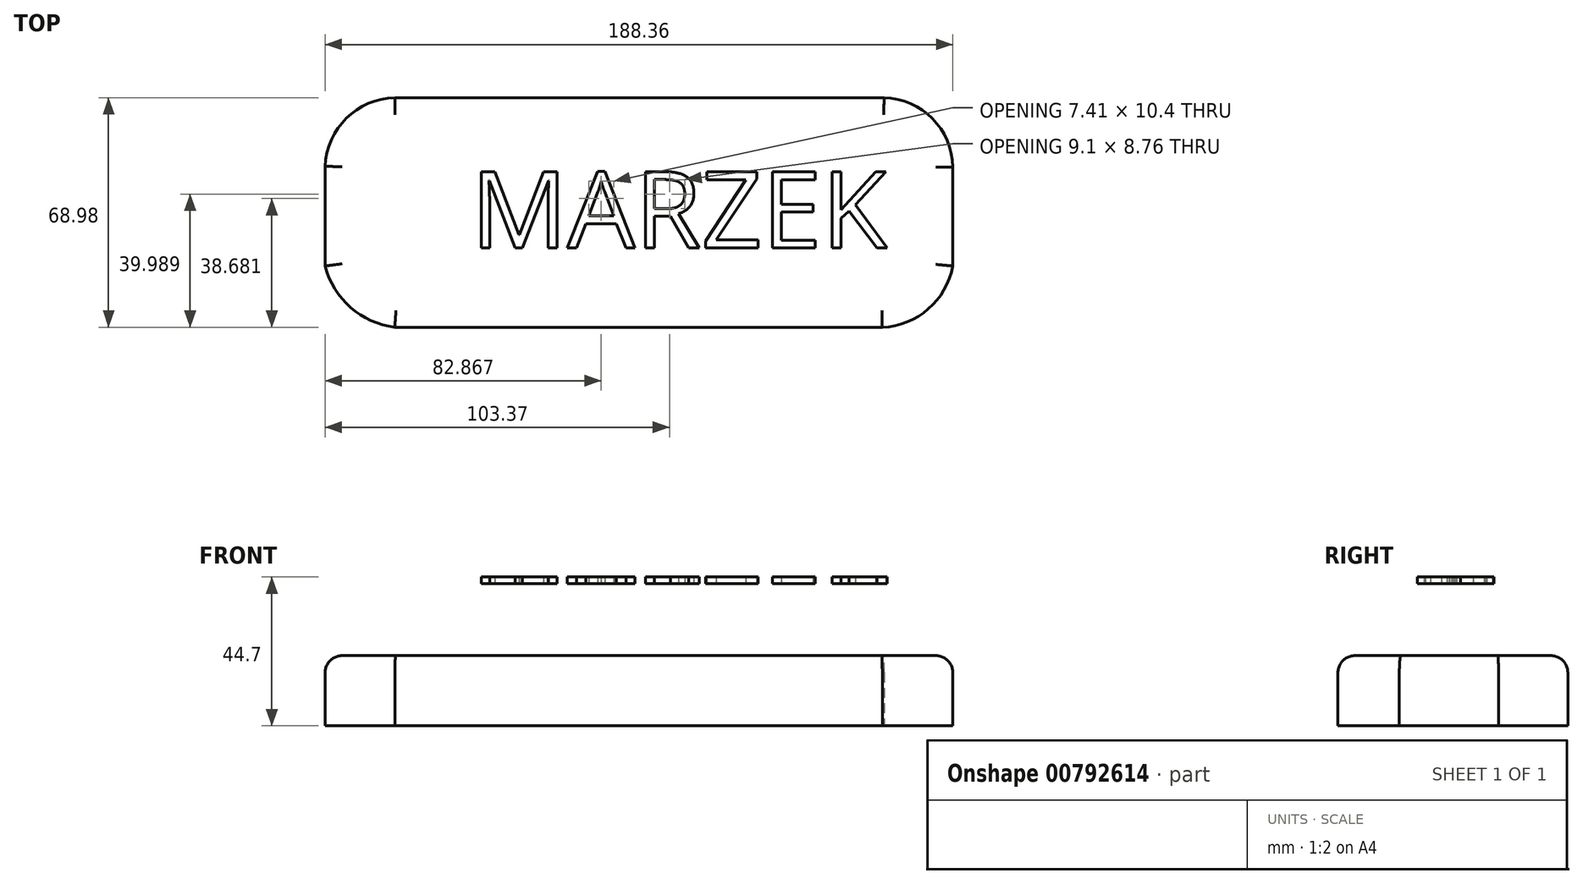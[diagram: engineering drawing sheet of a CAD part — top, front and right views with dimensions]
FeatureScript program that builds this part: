
annotation { "Feature Type Name" : "Feature", "Feature Type Description" : "" }
export const myFeature = defineFeature(function(context is Context, id is Id, definition is map)
    precondition{}
    {
        {
            var Q0;
            Q0=qCreatedBy(makeId("Top.planeOp"),FACE);
            var sketch = newSketch(context, id + "F0", { "sketchPlane" : qUnion([Q0])});
            skLineSegment(sketch, "E0.bottom", {"start": v(-94.18, 34.5) * mm, "end": v(94.18, 34.5) * mm});
            skLineSegment(sketch, "E0.top", {"start": v(-94.18, -34.5) * mm, "end": v(94.18, -34.5) * mm});
            skLineSegment(sketch, "E0.left", {"start": v(-94.18, 34.5) * mm, "end": v(-94.18, -34.5) * mm});
            skLineSegment(sketch, "E0.right", {"start": v(94.18, 34.5) * mm, "end": v(94.18, -34.5) * mm});
            skPoint(sketch, "E0.middle", {"position": v(0, 0) * mm});
            skArc(sketch, "E1", {"start": v(-73.27, 34.5) * mm, "mid": v(-88.4, 27.7) * mm, "end": v(-94.18, 12.16) * mm});
            skArc(sketch, "E2", {"start": v(94.18, 13) * mm, "mid": v(88.29, 28) * mm, "end": v(73.55, 34.5) * mm});
            skArc(sketch, "E3", {"start": v(-94.18, -16.07) * mm, "mid": v(-86.56, -28.5) * mm, "end": v(-73.27, -34.5) * mm});
            skArc(sketch, "E4", {"start": v(73.02, -34.5) * mm, "mid": v(86.83, -28.99) * mm, "end": v(94.18, -16.07) * mm});
            skSolve(sketch);
        }
        {
            var Q0;
            {var subQ3=sQuery(id+"F0.wireOp",EDGE,"E3");Q0=makeQuery(id+"F0.imprint","IMPRINT",FACE,{"disambiguationData":[TD([[makeQuery(id+"F0.imprint","IMPRINT",EDGE,{"derivedFrom":subQ3}),1.0]])]});}
            extrude(context, id + "F1", {"entities" : qUnion([Q0]), "depth" : 8.38 * mm, "offsetDistance" : 25.4 * mm});
        }
        {
            var Q0;
            Q0=makeQuery(id+"F1.opExtrude","CAP_FACE",FACE,{"disambiguationData":[OSD([sQuery(id+"F0.wireOp",EDGE,"E0.bottom"),sQuery(id+"F0.wireOp",EDGE,"E0.top"),sQuery(id+"F0.wireOp",EDGE,"E0.left"),sQuery(id+"F0.wireOp",EDGE,"E0.right"),sQuery(id+"F0.wireOp",EDGE,"E1"),sQuery(id+"F0.wireOp",EDGE,"E2"),sQuery(id+"F0.wireOp",EDGE,"E3"),sQuery(id+"F0.wireOp",EDGE,"E4")])],"isStart":false});
            extrude(context, id + "F2", {"entities" : qUnion([Q0]), "operationType" : NewBodyOperationType.ADD, "depth" : 25.4 * mm, "offsetDistance" : 25.4 * mm});
        }
        {
            var Q0;
            Q0=makeQuery(id+"F2.opExtrude","CAP_EDGE",EDGE,{"disambiguationData":[OSD([sQuery(id+"F0.wireOp",EDGE,"E0.bottom")])],"isStart":false});
            var Q1;
            Q1=makeQuery(id+"F2.opExtrude","CAP_EDGE",EDGE,{"disambiguationData":[OSD([sQuery(id+"F0.wireOp",EDGE,"E1")])],"isStart":false});
            var Q2;
            Q2=makeQuery(id+"F2.opExtrude","CAP_EDGE",EDGE,{"disambiguationData":[OSD([sQuery(id+"F0.wireOp",EDGE,"E0.left")])],"isStart":false});
            var Q3;
            Q3=makeQuery(id+"F2.opExtrude","CAP_EDGE",EDGE,{"disambiguationData":[OSD([sQuery(id+"F0.wireOp",EDGE,"E0.top")])],"isStart":false});
            var Q4;
            Q4=makeQuery(id+"F2.opExtrude","CAP_EDGE",EDGE,{"disambiguationData":[OSD([sQuery(id+"F0.wireOp",EDGE,"E3")])],"isStart":false});
            var Q5;
            Q5=makeQuery(id+"F2.opExtrude","CAP_EDGE",EDGE,{"disambiguationData":[OSD([sQuery(id+"F0.wireOp",EDGE,"E0.right")])],"isStart":false});
            var Q6;
            Q6=makeQuery(id+"F2.opExtrude","CAP_EDGE",EDGE,{"disambiguationData":[OSD([sQuery(id+"F0.wireOp",EDGE,"E4")])],"isStart":false});
            var Q7;
            Q7=makeQuery(id+"F2.opExtrude","CAP_EDGE",EDGE,{"disambiguationData":[OSD([sQuery(id+"F0.wireOp",EDGE,"E2")])],"isStart":false});
            fillet(context, id + "F3", {"entities" : qUnion([Q0, Q1, Q2, Q3, Q4, Q5, Q6, Q7]), "radius" : 5.08 * mm, "tangentPropagation" : true, "allowEdgeOverflow" : false});
        }
        {
            var Q0;
            Q0=makeQuery(id+"F1.opExtrude","CAP_FACE",FACE,{"disambiguationData":[OSD([sQuery(id+"F0.wireOp",EDGE,"E0.bottom"),sQuery(id+"F0.wireOp",EDGE,"E0.top"),sQuery(id+"F0.wireOp",EDGE,"E0.left"),sQuery(id+"F0.wireOp",EDGE,"E0.right"),sQuery(id+"F0.wireOp",EDGE,"E1"),sQuery(id+"F0.wireOp",EDGE,"E2"),sQuery(id+"F0.wireOp",EDGE,"E3"),sQuery(id+"F0.wireOp",EDGE,"E4")])],"isStart":true});
            extrude(context, id + "F4", {"entities" : qUnion([Q0]), "operationType" : NewBodyOperationType.REMOVE, "oppositeDirection" : true, "depth" : 12.7 * mm, "offsetDistance" : 25.4 * mm});
        }
        {
            var Q0;
            Q0=qCreatedBy(makeId("Top.planeOp"),FACE);
            cPlane(context, id + "F5", {"entities" : qUnion([Q0]), "cplaneType" : CPlaneType.OFFSET, "offset" : 55.37 * mm, "width" : 152.4 * mm, "height" : 152.4 * mm});
        }
        {
            var Q0;
            Q0=qCreatedBy(id+"F5.planeOp",FACE);
            var sketch = newSketch(context, id + "F6", { "sketchPlane" : qUnion([Q0])});
            skText(sketch, "E5", { "text": "MARZEK", "fontName": "OpenSans-Regular.ttf"});
            const initialGuessF6  = {"E5": [-0.05044, -0.01069, 1, 0, 0.0231]};
            skSetInitialGuess(sketch, initialGuessF6);
            skSolve(sketch);
        }
        {
            var Q0;
            Q0 = qSketchRegion(id + "F6", true);
            extrude(context, id + "F7", {"entities" : qUnion([Q0]), "depth" : 2.03 * mm, "offsetDistance" : 25.4 * mm});
        }
    });
